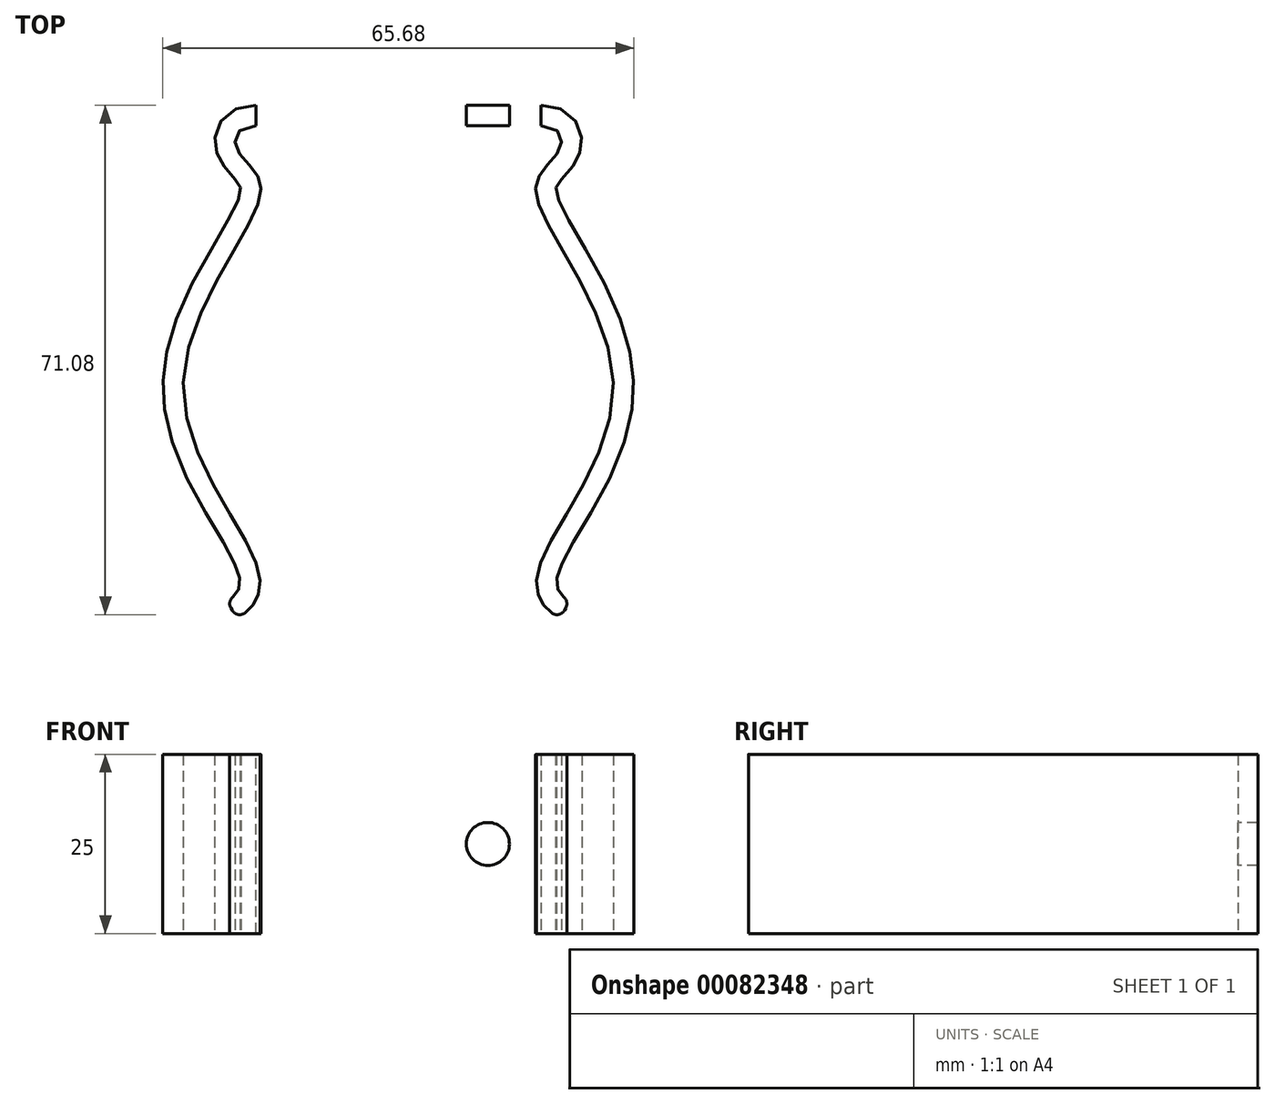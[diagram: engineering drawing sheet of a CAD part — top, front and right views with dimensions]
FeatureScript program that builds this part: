
annotation { "Feature Type Name" : "Feature", "Feature Type Description" : "" }
export const myFeature = defineFeature(function(context is Context, id is Id, definition is map)
    precondition{}
    {
        {
            var Q0;
            Q0=qCreatedBy(makeId("Top.planeOp"),FACE);
            var sketch = newSketch(context, id + "F0", { "sketchPlane" : qUnion([Q0])});
            skLineSegment(sketch, "E0", {"start": v(0, 0) * mm, "end": v(-19.88, 0) * mm});
            skFitSpline(sketch, "E1", {"points": [v(-19.88, 0) * mm, v(-22.72, -2.72) * mm, v(-19.88, -6.64) * mm, v(-19.88, -11.76) * mm, v(-30, -36.7) * mm, v(-19.88, -60.94) * mm, v(-19.88, -66.28) * mm, v(-22.56, -68.78) * mm], "startDerivative": vector(-76.7, 0) * mm, "endDerivative": vector(-42.67, -23.3) * mm});
            skLineSegment(sketch, "E2.MirrorCS", {"start": v(0, 0) * mm, "end": v(19.88, 0) * mm});
            skFitSpline(sketch, "E3.MirrorCS", {"points": [v(19.88, 0) * mm, v(22.72, -2.72) * mm, v(19.88, -6.64) * mm, v(19.88, -11.76) * mm, v(30, -36.7) * mm, v(19.88, -60.94) * mm, v(19.88, -66.28) * mm, v(22.56, -68.78) * mm], "startDerivative": vector(76.7, 0) * mm, "endDerivative": vector(42.67, -23.3) * mm});
            skFitSpline(sketch, "E4.0", {"points": [v(-19.88, 2.8) * mm, v(-20.46, 2.8) * mm, v(-21.59, 2.69) * mm, v(-22.9, 2.2) * mm, v(-23.83, 1.57) * mm, v(-24.44, 0.99) * mm, v(-24.92, 0.32) * mm, v(-25.28, -0.4) * mm, v(-25.5, -1.15) * mm, v(-25.6, -1.9) * mm, v(-25.58, -2.62) * mm, v(-25.5, -3.2) * mm, v(-25.37, -3.65) * mm, v(-25.23, -4.07) * mm, v(-25.02, -4.55) * mm, v(-24.74, -5.06) * mm, v(-24.34, -5.67) * mm, v(-23.83, -6.3) * mm, v(-23.26, -6.95) * mm, v(-22.84, -7.41) * mm, v(-22.56, -7.73) * mm, v(-22.39, -7.94) * mm, v(-22.25, -8.12) * mm, v(-22.13, -8.3) * mm, v(-22.04, -8.48) * mm, v(-22, -8.63) * mm, v(-21.96, -8.8) * mm, v(-21.97, -9.08) * mm, v(-22.04, -9.51) * mm, v(-22.23, -10.13) * mm, v(-22.55, -10.92) * mm, v(-23.03, -11.9) * mm, v(-23.85, -13.41) * mm, v(-25.12, -15.62) * mm, v(-26.9, -18.65) * mm, v(-28.71, -22.02) * mm, v(-30.41, -25.65) * mm, v(-31.58, -28.87) * mm, v(-32.27, -31.55) * mm, v(-32.63, -33.6) * mm, v(-32.82, -35.7) * mm, v(-32.8, -37.84) * mm, v(-32.56, -39.92) * mm, v(-32, -42.63) * mm, v(-30.95, -45.87) * mm, v(-29.32, -49.52) * mm, v(-27.5, -52.9) * mm, v(-25.7, -56) * mm, v(-24.34, -58.28) * mm, v(-23.45, -59.88) * mm, v(-22.9, -60.96) * mm, v(-22.57, -61.73) * mm, v(-22.38, -62.25) * mm, v(-22.23, -62.72) * mm, v(-22.11, -63.23) * mm, v(-22.06, -63.72) * mm, v(-22.07, -64.1) * mm, v(-22.12, -64.4) * mm, v(-22.19, -64.62) * mm, v(-22.26, -64.79) * mm, v(-22.32, -64.92) * mm, v(-22.39, -65.05) * mm, v(-22.48, -65.2) * mm, v(-22.61, -65.37) * mm, v(-22.8, -65.57) * mm, v(-23.16, -65.87) * mm, v(-23.56, -66.13) * mm, v(-23.9, -66.32) * mm]});
            skLineSegment(sketch, "E4.1", {"start": v(0, 2.8) * mm, "end": v(-19.88, 2.8) * mm});
            skLineSegment(sketch, "E4.2", {"start": v(0, 2.8) * mm, "end": v(19.88, 2.8) * mm});
            skFitSpline(sketch, "E4.3", {"points": [v(19.88, 2.8) * mm, v(20.46, 2.8) * mm, v(21.59, 2.69) * mm, v(22.9, 2.2) * mm, v(23.83, 1.57) * mm, v(24.44, 0.99) * mm, v(24.92, 0.32) * mm, v(25.28, -0.4) * mm, v(25.5, -1.15) * mm, v(25.6, -1.9) * mm, v(25.58, -2.62) * mm, v(25.5, -3.2) * mm, v(25.37, -3.65) * mm, v(25.23, -4.07) * mm, v(25.02, -4.55) * mm, v(24.74, -5.06) * mm, v(24.34, -5.67) * mm, v(23.83, -6.3) * mm, v(23.26, -6.95) * mm, v(22.84, -7.41) * mm, v(22.56, -7.73) * mm, v(22.39, -7.94) * mm, v(22.25, -8.12) * mm, v(22.13, -8.3) * mm, v(22.04, -8.48) * mm, v(22, -8.63) * mm, v(21.96, -8.8) * mm, v(21.97, -9.08) * mm, v(22.04, -9.51) * mm, v(22.23, -10.13) * mm, v(22.55, -10.92) * mm, v(23.03, -11.9) * mm, v(23.85, -13.41) * mm, v(25.12, -15.62) * mm, v(26.9, -18.65) * mm, v(28.71, -22.02) * mm, v(30.41, -25.65) * mm, v(31.58, -28.87) * mm, v(32.27, -31.55) * mm, v(32.63, -33.6) * mm, v(32.82, -35.7) * mm, v(32.8, -37.84) * mm, v(32.56, -39.92) * mm, v(32, -42.63) * mm, v(30.95, -45.87) * mm, v(29.32, -49.52) * mm, v(27.5, -52.9) * mm, v(25.7, -56) * mm, v(24.34, -58.28) * mm, v(23.45, -59.88) * mm, v(22.9, -60.96) * mm, v(22.57, -61.73) * mm, v(22.38, -62.25) * mm, v(22.23, -62.72) * mm, v(22.11, -63.23) * mm, v(22.06, -63.72) * mm, v(22.07, -64.1) * mm, v(22.12, -64.4) * mm, v(22.19, -64.62) * mm, v(22.26, -64.79) * mm, v(22.32, -64.92) * mm, v(22.39, -65.05) * mm, v(22.48, -65.2) * mm, v(22.61, -65.37) * mm, v(22.8, -65.57) * mm, v(23.16, -65.87) * mm, v(23.56, -66.13) * mm, v(23.9, -66.32) * mm]});
            skLineSegment(sketch, "E5", {"start": v(-23.9, -66.32) * mm, "end": v(-22.56, -68.78) * mm});
            skLineSegment(sketch, "E6", {"start": v(22.56, -68.78) * mm, "end": v(23.9, -66.32) * mm});
            skSolve(sketch);
        }
        {
            var Q0;
            Q0 = qSketchRegion(id + "F0", true);
            extrude(context, id + "F1", {"entities" : qUnion([Q0]), "depth" : 25 * mm, "offsetDistance" : 25 * mm});
        }
        {
            var Q0;
            Q0=makeQuery(id+"F1.opExtrude","SWEPT_FACE",FACE,{"disambiguationData":[OSD([sQuery(id+"F0.wireOp",EDGE,"E0"),sQuery(id+"F0.wireOp",EDGE,"E2.MirrorCS")])]});
            var sketch = newSketch(context, id + "F2", { "sketchPlane" : qUnion([Q0])});
            skCircle(sketch, "E7", {"center": v(-12.5, 12.5) * mm, "radius": 3 * mm});
            skCircle(sketch, "E8.MirrorC", {"center": v(12.5, 12.5) * mm, "radius": 3 * mm});
            skSolve(sketch);
        }
        {
            var Q0;
            Q0=makeQuery(id+"F2.imprint","IMPRINT",FACE,{"disambiguationData":[TD([[makeQuery(id+"F2.imprint","IMPRINT",EDGE,{"derivedFrom":sQuery(id+"F2.wireOp",EDGE,"E7")}),1.0]])]});
            var Q1;
            Q1=makeQuery(id+"F2.imprint","IMPRINT",FACE,{"disambiguationData":[TD([[makeQuery(id+"F2.imprint","IMPRINT",EDGE,{"derivedFrom":sQuery(id+"F2.wireOp",EDGE,"E8.MirrorC")}),-1.0]])]});
            extrude(context, id + "F3", {"entities" : qUnion([Q0, Q1]), "operationType" : NewBodyOperationType.REMOVE, "oppositeDirection" : true, "depth" : 25 * mm, "offsetDistance" : 25 * mm});
        }
        {
            var Q0;
            Q0=makeQuery(id+"F1.opExtrude","SWEPT_EDGE",EDGE,{"disambiguationData":[OSD([sQuery(id+"F0.wireOp",EDGE,"E1"),sQuery(id+"F0.wireOp",EDGE,"E5")])]});
            var Q1;
            Q1=makeQuery(id+"F1.opExtrude","SWEPT_EDGE",EDGE,{"disambiguationData":[OSD([sQuery(id+"F0.wireOp",EDGE,"E4.0"),sQuery(id+"F0.wireOp",EDGE,"E5")])]});
            var Q2;
            Q2=makeQuery(id+"F1.opExtrude","SWEPT_EDGE",EDGE,{"disambiguationData":[OSD([sQuery(id+"F0.wireOp",EDGE,"E3.MirrorCS"),sQuery(id+"F0.wireOp",EDGE,"E6")])]});
            var Q3;
            Q3=makeQuery(id+"F1.opExtrude","SWEPT_EDGE",EDGE,{"disambiguationData":[OSD([sQuery(id+"F0.wireOp",EDGE,"E4.3"),sQuery(id+"F0.wireOp",EDGE,"E6")])]});
            fillet(context, id + "F4", {"entities" : qUnion([Q0, Q1, Q2, Q3]), "radius" : 1.2 * mm, "tangentPropagation" : true, "allowEdgeOverflow" : false});
        }
    });
